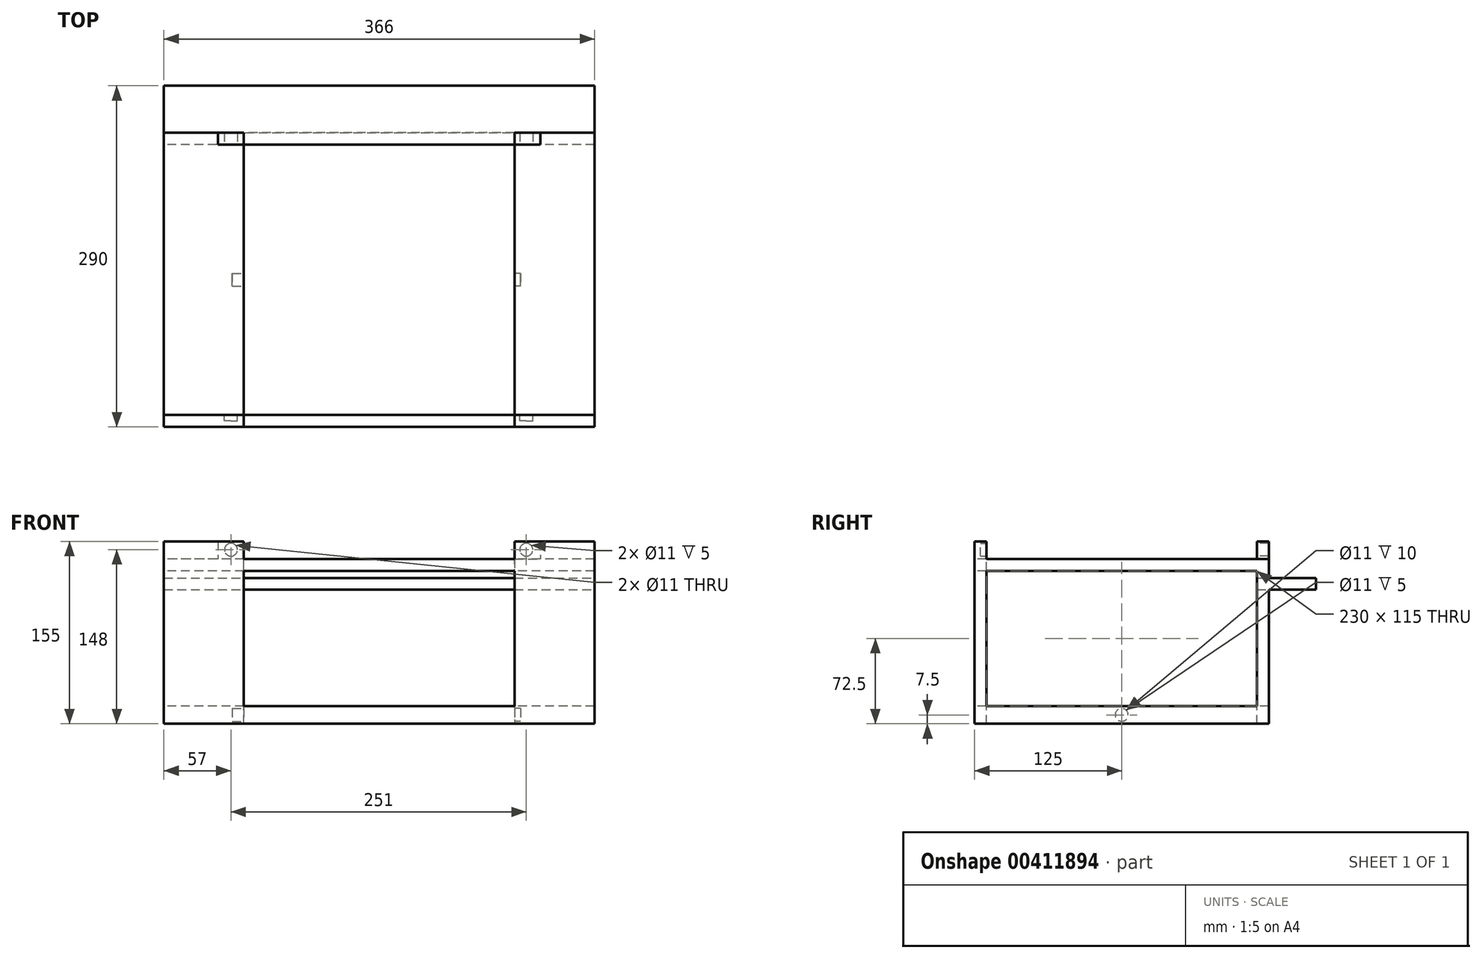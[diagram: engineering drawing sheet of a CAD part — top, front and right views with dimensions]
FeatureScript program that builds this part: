
annotation { "Feature Type Name" : "Feature", "Feature Type Description" : "" }
export const myFeature = defineFeature(function(context is Context, id is Id, definition is map)
    precondition{}
    {
        {
            var Q0;
            Q0=qCreatedBy(makeId("Top.planeOp"),FACE);
            var sketch = newSketch(context, id + "F0", { "sketchPlane" : qUnion([Q0])});
            skLineSegment(sketch, "E0.bottom", {"start": v(-183, 125) * mm, "end": v(183, 125) * mm});
            skLineSegment(sketch, "E0.top", {"start": v(-183, -125) * mm, "end": v(183, -125) * mm});
            skLineSegment(sketch, "E0.left", {"start": v(-183, 125) * mm, "end": v(-183, -125) * mm});
            skLineSegment(sketch, "E0.right", {"start": v(183, 125) * mm, "end": v(183, -125) * mm});
            skSolve(sketch);
        }
        {
            var Q0;
            Q0 = qSketchRegion(id + "F0", true);
            extrude(context, id + "F1", {"entities" : qUnion([Q0]), "depth" : 155 * mm});
        }
        {
            var Q0;
            Q0=makeQuery(id+"F1.opExtrude","CAP_FACE",FACE,{"disambiguationData":[OSD([sQuery(id+"F0.wireOp",EDGE,"E0.bottom"),sQuery(id+"F0.wireOp",EDGE,"E0.top"),sQuery(id+"F0.wireOp",EDGE,"E0.left"),sQuery(id+"F0.wireOp",EDGE,"E0.right")])],"isStart":false});
            shell(context, id + "F2", {"entities" : qUnion([Q0]), "thickness" : 10 * mm});
        }
        {
            var Q0;
            Q0=makeQuery(id+"F2.opShell","OFFSET_FACE",FACE,{"disambiguationData":[OSD([sQuery(id+"F0.wireOp",EDGE,"E0.bottom"),sQuery(id+"F0.wireOp",EDGE,"E0.top"),sQuery(id+"F0.wireOp",EDGE,"E0.left"),sQuery(id+"F0.wireOp",EDGE,"E0.right")])]});
            var sketch = newSketch(context, id + "F3", { "sketchPlane" : qUnion([Q0])});
            skSolve(sketch);
        }
        {
            var Q0;
            Q0 = qSketchRegion(id + "F3", true);
            var Q1;
            {var subQ0=sQuery(id+"F0.wireOp",EDGE,"E0.bottom");Q1=makeQuery(id+"F3.imprint","IMPRINT",FACE,{"disambiguationData":[TD([[makeQuery(id+"F3.imprint","IMPRINT",EDGE,{"derivedFrom":makeQuery(id+"F2.opShell","OFFSET_EDGE",EDGE,{"disambiguationData":[OSD([subQ0]),TDD([makeQuery(id+"F1.opExtrude","CAP_EDGE",EDGE,{"disambiguationData":[OSD([subQ0])],"isStart":true})])]})}),-1.0]])]});}
            extrude(context, id + "F4", {"entities" : qUnion([Q0, Q1]), "operationType" : NewBodyOperationType.REMOVE, "oppositeDirection" : true, "depth" : 25 * mm});
        }
        {
            var Q0;
            Q0=makeQuery(id+"F1.opExtrude","SWEPT_FACE",FACE,{"disambiguationData":[OSD([sQuery(id+"F0.wireOp",EDGE,"E0.top")])]});
            var sketch = newSketch(context, id + "F5", { "sketchPlane" : qUnion([Q0])});
            skLineSegment(sketch, "E1", {"start": v(0, 0) * mm, "end": v(0, 92.09) * mm});
            skLineSegment(sketch, "E2.bottom", {"start": v(-115, 130) * mm, "end": v(115, 130) * mm});
            skLineSegment(sketch, "E2.top", {"start": v(-115, 15) * mm, "end": v(115, 15) * mm});
            skLineSegment(sketch, "E2.left", {"start": v(-115, 130) * mm, "end": v(-115, 15) * mm});
            skLineSegment(sketch, "E2.right", {"start": v(115, 130) * mm, "end": v(115, 15) * mm});
            skLineSegment(sketch, "E3.bottom", {"start": v(-115, 155) * mm, "end": v(115, 155) * mm});
            skLineSegment(sketch, "E3.top", {"start": v(-115, 140) * mm, "end": v(115, 140) * mm});
            skLineSegment(sketch, "E3.left", {"start": v(-115, 155) * mm, "end": v(-115, 140) * mm});
            skLineSegment(sketch, "E3.right", {"start": v(115, 155) * mm, "end": v(115, 140) * mm});
            skSolve(sketch);
        }
        {
            var Q0;
            Q0 = qSketchRegion(id + "F5", true);
            extrude(context, id + "F6", {"entities" : qUnion([Q0]), "operationType" : NewBodyOperationType.REMOVE, "oppositeDirection" : true, "depth" : 500 * mm});
        }
        {
            var Q0;
            Q0=makeQuery(id+"F1.opExtrude","SWEPT_FACE",FACE,{"disambiguationData":[OSD([sQuery(id+"F0.wireOp",EDGE,"E0.left")])]});
            var sketch = newSketch(context, id + "F7", { "sketchPlane" : qUnion([Q0])});
            skLineSegment(sketch, "E4", {"start": v(0, 0) * mm, "end": v(0, 112.83) * mm});
            skLineSegment(sketch, "E5.bottom", {"start": v(-115, 130) * mm, "end": v(115, 130) * mm});
            skLineSegment(sketch, "E5.top", {"start": v(-115, 15) * mm, "end": v(115, 15) * mm});
            skLineSegment(sketch, "E5.left", {"start": v(-115, 130) * mm, "end": v(-115, 15) * mm});
            skLineSegment(sketch, "E5.right", {"start": v(115, 130) * mm, "end": v(115, 15) * mm});
            skLineSegment(sketch, "E6.bottom", {"start": v(-125, 114) * mm, "end": v(-125, 114) * mm});
            skLineSegment(sketch, "E6.top", {"start": v(-125, 0) * mm, "end": v(-125, 0) * mm});
            skLineSegment(sketch, "E7.bottom", {"start": v(-125, 155) * mm, "end": v(115, 155) * mm});
            skLineSegment(sketch, "E7.top", {"start": v(-125, 140) * mm, "end": v(115, 140) * mm});
            skLineSegment(sketch, "E7.left", {"start": v(-125, 155) * mm, "end": v(-125, 140) * mm});
            skLineSegment(sketch, "E7.right", {"start": v(115, 155) * mm, "end": v(115, 140) * mm});
            skSolve(sketch);
        }
        {
            var Q0;
            Q0=makeQuery(id+"F7.imprint","IMPRINT",FACE,{"disambiguationData":[TD([[makeQuery(id+"F7.imprint","IMPRINT",EDGE,{"derivedFrom":sQuery(id+"F7.wireOp",EDGE,"E7.bottom")}),-1.0]])]});
            var Q1;
            Q1=makeQuery(id+"F7.imprint","IMPRINT",FACE,{"disambiguationData":[TD([[makeQuery(id+"F7.imprint","IMPRINT",EDGE,{"derivedFrom":sQuery(id+"F7.wireOp",EDGE,"E5.bottom")}),-1.0]])]});
            extrude(context, id + "F8", {"entities" : qUnion([Q0, Q1]), "operationType" : NewBodyOperationType.REMOVE, "oppositeDirection" : true, "depth" : 500 * mm});
        }
        {
            var Q0;
            Q0=makeQuery(id+"F1.opExtrude","SWEPT_FACE",FACE,{"disambiguationData":[OSD([sQuery(id+"F0.wireOp",EDGE,"E0.left")])]});
            var sketch = newSketch(context, id + "F9", { "sketchPlane" : qUnion([Q0])});
            skLineSegment(sketch, "E8.bottom", {"start": v(-115, 124) * mm, "end": v(-165, 124) * mm});
            skLineSegment(sketch, "E8.top", {"start": v(-115, 114) * mm, "end": v(-165, 114) * mm});
            skLineSegment(sketch, "E8.left", {"start": v(-115, 124) * mm, "end": v(-115, 114) * mm});
            skLineSegment(sketch, "E8.right", {"start": v(-165, 124) * mm, "end": v(-165, 114) * mm});
            skLineSegment(sketch, "E9.0", {"start": v(115, 155) * mm, "end": v(125, 155) * mm});
            skLineSegment(sketch, "E10.0", {"start": v(125, 155) * mm, "end": v(125, 0) * mm});
            skSolve(sketch);
        }
        {
            var Q0;
            Q0 = qSketchRegion(id + "F9", true);
            var Q1;
            Q1=makeQuery(id+"F1.opExtrude","SWEPT_FACE",FACE,{"disambiguationData":[OSD([sQuery(id+"F0.wireOp",EDGE,"E0.right")])]});
            extrude(context, id + "F10", {"entities" : qUnion([Q0]), "operationType" : NewBodyOperationType.ADD, "endBound" : BoundingType.UP_TO_SURFACE, "oppositeDirection" : true, "endBoundEntityFace" : qUnion([Q1]), "depth" : 25 * mm});
        }
        {
            var Q0;
            {var subQ0=sQuery(id+"F0.wireOp",EDGE,"E0.bottom");var subQ1=makeQuery(id+"F1.opExtrude","SWEPT_FACE",FACE,{"disambiguationData":[OSD([subQ0])]});var subQ9=sQuery(id+"F9.wireOp",EDGE,"E8.bottom");Q0=makeQuery(id+"F10.boolean.opBoolean","SPLIT",FACE,{"disambiguationData":[TD([makeQuery(id+"F10.opExtrude","SWEPT_FACE",FACE,{"disambiguationData":[OSD([subQ9])]})])],"derivedFrom":subQ1});}
            var sketch = newSketch(context, id + "F11", { "sketchPlane" : qUnion([Q0])});
            skLineSegment(sketch, "E11.bottom", {"start": v(-115, 124) * mm, "end": v(115, 124) * mm});
            skLineSegment(sketch, "E11.top", {"start": v(-115, 150.02) * mm, "end": v(115, 150.02) * mm});
            skLineSegment(sketch, "E11.left", {"start": v(-115, 124) * mm, "end": v(-115, 150.02) * mm});
            skLineSegment(sketch, "E11.right", {"start": v(115, 124) * mm, "end": v(115, 150.02) * mm});
            skSolve(sketch);
        }
        {
            var Q0;
            {var subQ0=sQuery(id+"F11.wireOp",EDGE,"E11.bottom");Q0=makeQuery(id+"F11.imprint","IMPRINT",FACE,{"disambiguationData":[TD([[makeQuery(id+"F11.imprint","IMPRINT",EDGE,{"derivedFrom":subQ0}),1.0]])]});}
            var Q1;
            {var subQ1=sQuery(id+"F0.wireOp",EDGE,"E0.bottom");var subQ2=makeQuery(id+"F1.opExtrude","SWEPT_FACE",FACE,{"disambiguationData":[OSD([subQ1])]});var subQ3=makeQuery(id+"F6.boolean.opBoolean","INTERSECT",EDGE,{"derivedFrom":[subQ2,makeQuery(id+"F6.opExtrude","SWEPT_FACE",FACE,{"disambiguationData":[OSD([sQuery(id+"F5.wireOp",EDGE,"E2.bottom")])]})]});Q1=makeQuery(id+"F11.imprint","IMPRINT",FACE,{"disambiguationData":[TD([[makeQuery(id+"F11.imprint","IMPRINT",EDGE,{"derivedFrom":subQ3}),1.0]])]});}
            extrude(context, id + "F12", {"entities" : qUnion([Q0, Q1]), "operationType" : NewBodyOperationType.REMOVE, "oppositeDirection" : true, "depth" : 200 * mm});
        }
        {
            var Q0;
            {var subQ0=sQuery(id+"F0.wireOp",EDGE,"E0.right");var subQ2=sQuery(id+"F0.wireOp",EDGE,"E0.bottom");var subQ4=makeQuery(id+"F1.opExtrude","SWEPT_FACE",FACE,{"disambiguationData":[OSD([subQ2])]});Q0=makeQuery(id+"F12.boolean.opBoolean","SPLIT",FACE,{"disambiguationData":[TD([makeQuery(id+"F1.opExtrude","SWEPT_FACE",FACE,{"disambiguationData":[OSD([subQ0])]})])],"derivedFrom":makeQuery(id+"F8.boolean.opBoolean","MERGE",FACE,{"derivedFrom":[makeQuery(id+"F6.boolean.opBoolean","COPY",FACE,{"disambiguationData":[TD([subQ4])],"derivedFrom":makeQuery(id+"F6.opExtrude","SWEPT_FACE",FACE,{"disambiguationData":[OSD([sQuery(id+"F5.wireOp",EDGE,"E3.top")])]})}),makeQuery(id+"F8.opExtrude","SWEPT_FACE",FACE,{"disambiguationData":[OSD([sQuery(id+"F7.wireOp",EDGE,"E7.top")])]})]})});}
            var sketch = newSketch(context, id + "F13", { "sketchPlane" : qUnion([Q0])});
            skLineSegment(sketch, "E12.bottom", {"start": v(115, 115) * mm, "end": v(137, 115) * mm});
            skLineSegment(sketch, "E12.top", {"start": v(115, 125) * mm, "end": v(137, 125) * mm});
            skLineSegment(sketch, "E12.left", {"start": v(115, 115) * mm, "end": v(115, 125) * mm});
            skLineSegment(sketch, "E12.right", {"start": v(137, 115) * mm, "end": v(137, 125) * mm});
            skSolve(sketch);
        }
        {
            var Q0;
            Q0=makeQuery(id+"F13.imprint","IMPRINT",FACE,{"disambiguationData":[TD([[makeQuery(id+"F13.imprint","IMPRINT",EDGE,{"derivedFrom":sQuery(id+"F13.wireOp",EDGE,"E12.bottom")}),-1.0]])]});
            extrude(context, id + "F14", {"entities" : qUnion([Q0]), "operationType" : NewBodyOperationType.ADD, "depth" : 15 * mm});
        }
        {
            var Q0;
            {var subQ0=sQuery(id+"F0.wireOp",EDGE,"E0.bottom");var subQ3=makeQuery(id+"F1.opExtrude","SWEPT_FACE",FACE,{"disambiguationData":[OSD([subQ0])]});var subQ4=sQuery(id+"F0.wireOp",EDGE,"E0.left");Q0=makeQuery(id+"F12.boolean.opBoolean","SPLIT",FACE,{"disambiguationData":[TD([makeQuery(id+"F1.opExtrude","SWEPT_FACE",FACE,{"disambiguationData":[OSD([subQ4])]})])],"derivedFrom":makeQuery(id+"F8.boolean.opBoolean","MERGE",FACE,{"derivedFrom":[makeQuery(id+"F6.boolean.opBoolean","COPY",FACE,{"disambiguationData":[TD([subQ3])],"derivedFrom":makeQuery(id+"F6.opExtrude","SWEPT_FACE",FACE,{"disambiguationData":[OSD([sQuery(id+"F5.wireOp",EDGE,"E3.top")])]})}),makeQuery(id+"F8.opExtrude","SWEPT_FACE",FACE,{"disambiguationData":[OSD([sQuery(id+"F7.wireOp",EDGE,"E7.top")])]})]})});}
            var sketch = newSketch(context, id + "F15", { "sketchPlane" : qUnion([Q0])});
            skLineSegment(sketch, "E13.bottom", {"start": v(-115, 115) * mm, "end": v(-137, 115) * mm});
            skLineSegment(sketch, "E13.top", {"start": v(-115, 125) * mm, "end": v(-137, 125) * mm});
            skLineSegment(sketch, "E13.left", {"start": v(-115, 115) * mm, "end": v(-115, 125) * mm});
            skLineSegment(sketch, "E13.right", {"start": v(-137, 115) * mm, "end": v(-137, 125) * mm});
            skSolve(sketch);
        }
        {
            var Q0;
            Q0=makeQuery(id+"F15.imprint","IMPRINT",FACE,{"disambiguationData":[TD([[makeQuery(id+"F15.imprint","IMPRINT",EDGE,{"derivedFrom":sQuery(id+"F15.wireOp",EDGE,"E13.bottom")}),-1.0]])]});
            extrude(context, id + "F16", {"entities" : qUnion([Q0]), "operationType" : NewBodyOperationType.ADD, "depth" : 15 * mm});
        }
        {
            var Q0;
            {var subQ4=sQuery(id+"F0.wireOp",EDGE,"E0.right");Q0=makeQuery(id+"F8.boolean.opBoolean","SPLIT",FACE,{"disambiguationData":[TD([makeQuery(id+"F8.opExtrude","SWEPT_FACE",FACE,{"disambiguationData":[OSD([sQuery(id+"F7.wireOp",EDGE,"E5.bottom")])]})])],"derivedFrom":makeQuery(id+"F4.boolean.opBoolean","MERGE",FACE,{"derivedFrom":[makeQuery(id+"F2.opShell","OFFSET_FACE",FACE,{"disambiguationData":[OSD([subQ4])]}),makeQuery(id+"F4.opExtrude","SWEPT_FACE",FACE,{"disambiguationData":[OSD([subQ4])]})]})});}
            var Q1;
            {var subQ0=sQuery(id+"F0.wireOp",EDGE,"E0.top");Q1=makeQuery(id+"F6.boolean.opBoolean","COPY",FACE,{"disambiguationData":[TD([makeQuery(id+"F1.opExtrude","SWEPT_FACE",FACE,{"disambiguationData":[OSD([subQ0])]})])],"derivedFrom":makeQuery(id+"F6.opExtrude","SWEPT_FACE",FACE,{"disambiguationData":[OSD([sQuery(id+"F5.wireOp",EDGE,"E2.right")])]})});}
            extrude(context, id + "F17", {"entities" : qUnion([Q0]), "operationType" : NewBodyOperationType.ADD, "endBound" : BoundingType.UP_TO_SURFACE, "endBoundEntityFace" : qUnion([Q1]), "depth" : 25 * mm});
        }
        {
            var Q0;
            {var subQ4=sQuery(id+"F0.wireOp",EDGE,"E0.left");Q0=makeQuery(id+"F8.boolean.opBoolean","SPLIT",FACE,{"disambiguationData":[TD([makeQuery(id+"F8.opExtrude","SWEPT_FACE",FACE,{"disambiguationData":[OSD([sQuery(id+"F7.wireOp",EDGE,"E5.bottom")])]})])],"derivedFrom":makeQuery(id+"F4.boolean.opBoolean","MERGE",FACE,{"derivedFrom":[makeQuery(id+"F2.opShell","OFFSET_FACE",FACE,{"disambiguationData":[OSD([subQ4])]}),makeQuery(id+"F4.opExtrude","SWEPT_FACE",FACE,{"disambiguationData":[OSD([subQ4])]})]})});}
            var Q1;
            {var subQ0=sQuery(id+"F0.wireOp",EDGE,"E0.top");Q1=makeQuery(id+"F6.boolean.opBoolean","COPY",FACE,{"disambiguationData":[TD([makeQuery(id+"F1.opExtrude","SWEPT_FACE",FACE,{"disambiguationData":[OSD([subQ0])]})])],"derivedFrom":makeQuery(id+"F6.opExtrude","SWEPT_FACE",FACE,{"disambiguationData":[OSD([sQuery(id+"F5.wireOp",EDGE,"E2.left")])]})});}
            extrude(context, id + "F18", {"entities" : qUnion([Q0]), "operationType" : NewBodyOperationType.ADD, "endBound" : BoundingType.UP_TO_SURFACE, "endBoundEntityFace" : qUnion([Q1]), "depth" : 25 * mm});
        }
        {
            var Q0;
            {var subQ2=sQuery(id+"F0.wireOp",EDGE,"E0.right");Q0=makeQuery(id+"F8.boolean.opBoolean","SPLIT",FACE,{"disambiguationData":[TD([makeQuery(id+"F8.opExtrude","SWEPT_FACE",FACE,{"disambiguationData":[OSD([sQuery(id+"F7.wireOp",EDGE,"E5.top")])]})])],"derivedFrom":makeQuery(id+"F4.boolean.opBoolean","MERGE",FACE,{"derivedFrom":[makeQuery(id+"F2.opShell","OFFSET_FACE",FACE,{"disambiguationData":[OSD([subQ2])]}),makeQuery(id+"F4.opExtrude","SWEPT_FACE",FACE,{"disambiguationData":[OSD([subQ2])]})]})});}
            var Q1;
            {var subQ0=sQuery(id+"F0.wireOp",EDGE,"E0.top");Q1=makeQuery(id+"F6.boolean.opBoolean","COPY",FACE,{"disambiguationData":[TD([makeQuery(id+"F1.opExtrude","SWEPT_FACE",FACE,{"disambiguationData":[OSD([subQ0])]})])],"derivedFrom":makeQuery(id+"F6.opExtrude","SWEPT_FACE",FACE,{"disambiguationData":[OSD([sQuery(id+"F5.wireOp",EDGE,"E2.right")])]})});}
            extrude(context, id + "F19", {"entities" : qUnion([Q0]), "operationType" : NewBodyOperationType.ADD, "endBound" : BoundingType.UP_TO_SURFACE, "endBoundEntityFace" : qUnion([Q1]), "depth" : 25 * mm});
        }
        {
            var Q0;
            {var subQ2=sQuery(id+"F0.wireOp",EDGE,"E0.left");Q0=makeQuery(id+"F8.boolean.opBoolean","SPLIT",FACE,{"disambiguationData":[TD([makeQuery(id+"F8.opExtrude","SWEPT_FACE",FACE,{"disambiguationData":[OSD([sQuery(id+"F7.wireOp",EDGE,"E5.top")])]})])],"derivedFrom":makeQuery(id+"F4.boolean.opBoolean","MERGE",FACE,{"derivedFrom":[makeQuery(id+"F2.opShell","OFFSET_FACE",FACE,{"disambiguationData":[OSD([subQ2])]}),makeQuery(id+"F4.opExtrude","SWEPT_FACE",FACE,{"disambiguationData":[OSD([subQ2])]})]})});}
            var Q1;
            {var subQ0=sQuery(id+"F0.wireOp",EDGE,"E0.top");Q1=makeQuery(id+"F6.boolean.opBoolean","COPY",FACE,{"disambiguationData":[TD([makeQuery(id+"F1.opExtrude","SWEPT_FACE",FACE,{"disambiguationData":[OSD([subQ0])]})])],"derivedFrom":makeQuery(id+"F6.opExtrude","SWEPT_FACE",FACE,{"disambiguationData":[OSD([sQuery(id+"F5.wireOp",EDGE,"E2.left")])]})});}
            extrude(context, id + "F20", {"entities" : qUnion([Q0]), "operationType" : NewBodyOperationType.ADD, "endBound" : BoundingType.UP_TO_SURFACE, "endBoundEntityFace" : qUnion([Q1]), "depth" : 25 * mm});
        }
        {
            var Q0;
            {var subQ2=sQuery(id+"F13.wireOp",EDGE,"E12.right");var subQ3=sQuery(id+"F13.wireOp",EDGE,"E12.bottom");var subQ4=sQuery(id+"F0.wireOp",EDGE,"E0.bottom");var subQ6=makeQuery(id+"F2.opShell","OFFSET_FACE",FACE,{"disambiguationData":[OSD([subQ4])]});Q0=makeQuery(id+"F17.boolean.opBoolean","SPLIT",FACE,{"disambiguationData":[TD([makeQuery(id+"F14.opExtrude","SWEPT_FACE",FACE,{"disambiguationData":[OSD([subQ2])]})])],"derivedFrom":makeQuery(id+"F16.boolean.opBoolean","MERGE",FACE,{"derivedFrom":[makeQuery(id+"F14.boolean.opBoolean","MERGE",FACE,{"derivedFrom":[makeQuery(id+"F10.boolean.opBoolean","MERGE",FACE,{"derivedFrom":[makeQuery(id+"F8.boolean.opBoolean","MERGE",FACE,{"derivedFrom":[makeQuery(id+"F4.boolean.opBoolean","MERGE",FACE,{"derivedFrom":[subQ6],"fromTools":[makeQuery(id+"F4.opExtrude","SWEPT_FACE",FACE,{"disambiguationData":[OSD([subQ4])]})]})],"fromTools":[makeQuery(id+"F8.opExtrude","SWEPT_FACE",FACE,{"disambiguationData":[OSD([sQuery(id+"F7.wireOp",EDGE,"E5.left")])]})]}),makeQuery(id+"F10.opExtrude","SWEPT_FACE",FACE,{"disambiguationData":[OSD([sQuery(id+"F9.wireOp",EDGE,"E8.left")])]})]}),makeQuery(id+"F14.opExtrude","SWEPT_FACE",FACE,{"disambiguationData":[OSD([subQ3])]})]}),makeQuery(id+"F16.opExtrude","SWEPT_FACE",FACE,{"disambiguationData":[OSD([sQuery(id+"F15.wireOp",EDGE,"E13.bottom")])]})]})});}
            var sketch = newSketch(context, id + "F21", { "sketchPlane" : qUnion([Q0])});
            skCircle(sketch, "E14", {"center": v(125, 148) * mm, "radius": 5.5 * mm});
            skLineSegment(sketch, "E15.0.0", {"start": v(115, 155) * mm, "end": v(115, 140) * mm});
            skLineSegment(sketch, "E15.0.1", {"start": v(115, 140) * mm, "end": v(137, 140) * mm});
            skLineSegment(sketch, "E15.0.2", {"start": v(137, 140) * mm, "end": v(137, 155) * mm});
            skLineSegment(sketch, "E15.0.3", {"start": v(137, 155) * mm, "end": v(115, 155) * mm});
            skSolve(sketch);
        }
        {
            var Q0;
            Q0=makeQuery(id+"F21.imprint","IMPRINT",FACE,{"disambiguationData":[TD([[makeQuery(id+"F21.imprint","IMPRINT",EDGE,{"derivedFrom":sQuery(id+"F21.wireOp",EDGE,"E14")}),1.0]])]});
            extrude(context, id + "F22", {"entities" : qUnion([Q0]), "operationType" : NewBodyOperationType.REMOVE, "depth" : 235 * mm});
        }
        {
            var Q0;
            {var subQ2=sQuery(id+"F0.wireOp",EDGE,"E0.bottom");var subQ4=makeQuery(id+"F2.opShell","OFFSET_FACE",FACE,{"disambiguationData":[OSD([subQ2])]});var subQ6=sQuery(id+"F15.wireOp",EDGE,"E13.right");var subQ7=makeQuery(id+"F16.opExtrude","SWEPT_FACE",FACE,{"disambiguationData":[OSD([subQ6])]});var subQ8=sQuery(id+"F15.wireOp",EDGE,"E13.bottom");var subQ14=sQuery(id+"F0.wireOp",EDGE,"E0.left");var subQ21=sQuery(id+"F9.wireOp",EDGE,"E8.left");var subQ26=makeQuery(id+"F8.opExtrude","SWEPT_FACE",FACE,{"disambiguationData":[OSD([sQuery(id+"F7.wireOp",EDGE,"E5.left")])]});var subQ30=makeQuery(id+"F1.opExtrude","SWEPT_FACE",FACE,{"disambiguationData":[OSD([subQ14])]});Q0=makeQuery(id+"F18.boolean.opBoolean","SPLIT",FACE,{"disambiguationData":[TD([subQ7])],"derivedFrom":makeQuery(id+"F17.boolean.opBoolean","SPLIT",FACE,{"disambiguationData":[TD([subQ30])],"derivedFrom":makeQuery(id+"F16.boolean.opBoolean","MERGE",FACE,{"derivedFrom":[makeQuery(id+"F14.boolean.opBoolean","MERGE",FACE,{"derivedFrom":[makeQuery(id+"F10.boolean.opBoolean","MERGE",FACE,{"derivedFrom":[makeQuery(id+"F8.boolean.opBoolean","MERGE",FACE,{"derivedFrom":[makeQuery(id+"F4.boolean.opBoolean","MERGE",FACE,{"derivedFrom":[subQ4],"fromTools":[makeQuery(id+"F4.opExtrude","SWEPT_FACE",FACE,{"disambiguationData":[OSD([subQ2])]})]})],"fromTools":[subQ26]}),makeQuery(id+"F10.opExtrude","SWEPT_FACE",FACE,{"disambiguationData":[OSD([subQ21])]})]}),makeQuery(id+"F14.opExtrude","SWEPT_FACE",FACE,{"disambiguationData":[OSD([sQuery(id+"F13.wireOp",EDGE,"E12.bottom")])]})]}),makeQuery(id+"F16.opExtrude","SWEPT_FACE",FACE,{"disambiguationData":[OSD([subQ8])]})]})})});}
            var sketch = newSketch(context, id + "F23", { "sketchPlane" : qUnion([Q0])});
            skCircle(sketch, "E16", {"center": v(-126, 148) * mm, "radius": 5.5 * mm});
            skPoint(sketch, "E16.centerSnap0", {"position": v(-126, 155) * mm});
            skLineSegment(sketch, "E17.0.0", {"start": v(-137, 140) * mm, "end": v(-115, 140) * mm});
            skLineSegment(sketch, "E17.0.1", {"start": v(-115, 140) * mm, "end": v(-115, 155) * mm});
            skLineSegment(sketch, "E17.0.2", {"start": v(-115, 155) * mm, "end": v(-137, 155) * mm});
            skLineSegment(sketch, "E17.0.3", {"start": v(-137, 155) * mm, "end": v(-137, 140) * mm});
            skSolve(sketch);
        }
        {
            var Q0;
            Q0=makeQuery(id+"F23.imprint","IMPRINT",FACE,{"disambiguationData":[TD([[makeQuery(id+"F23.imprint","IMPRINT",EDGE,{"derivedFrom":sQuery(id+"F23.wireOp",EDGE,"E16")}),1.0]])]});
            extrude(context, id + "F24", {"entities" : qUnion([Q0]), "operationType" : NewBodyOperationType.REMOVE, "oppositeDirection" : true, "depth" : 25 * mm});
        }
        {
            var Q0;
            Q0=makeQuery(id+"F19.opExtrude","CAP_FACE",FACE,{"disambiguationData":[OSD([sQuery(id+"F0.wireOp",EDGE,"E0.right")])],"isStart":false});
            var sketch = newSketch(context, id + "F25", { "sketchPlane" : qUnion([Q0])});
            skCircle(sketch, "E18", {"center": v(0, 7.5) * mm, "radius": 5.5 * mm});
            skLineSegment(sketch, "E19.0.0", {"start": v(-125, 140) * mm, "end": v(-125, 124) * mm});
            skLineSegment(sketch, "E19.0.1", {"start": v(-125, 124) * mm, "end": v(-165, 124) * mm});
            skLineSegment(sketch, "E19.0.2", {"start": v(-165, 124) * mm, "end": v(-165, 114) * mm});
            skLineSegment(sketch, "E19.0.3", {"start": v(-165, 114) * mm, "end": v(-125, 114) * mm});
            skLineSegment(sketch, "E19.0.4", {"start": v(-125, 114) * mm, "end": v(-125, 0) * mm});
            skLineSegment(sketch, "E19.0.5", {"start": v(-125, 0) * mm, "end": v(125, 0) * mm});
            skLineSegment(sketch, "E19.0.6", {"start": v(125, 0) * mm, "end": v(125, 155) * mm});
            skLineSegment(sketch, "E19.0.7", {"start": v(125, 155) * mm, "end": v(115, 155) * mm});
            skLineSegment(sketch, "E19.0.8", {"start": v(115, 155) * mm, "end": v(115, 140) * mm});
            skLineSegment(sketch, "E19.0.9", {"start": v(115, 140) * mm, "end": v(-125, 140) * mm});
            skSolve(sketch);
        }
        {
            var Q0;
            Q0=makeQuery(id+"F25.imprint","IMPRINT",FACE,{"disambiguationData":[TD([[makeQuery(id+"F25.imprint","IMPRINT",EDGE,{"derivedFrom":sQuery(id+"F25.wireOp",EDGE,"E18")}),1.0]])]});
            extrude(context, id + "F26", {"entities" : qUnion([Q0]), "operationType" : NewBodyOperationType.REMOVE, "depth" : 240 * mm});
        }
        {
            var Q0;
            Q0=makeQuery(id+"F22.boolean.opBoolean","COPY",FACE,{"derivedFrom":makeQuery(id+"F22.opExtrude","CAP_FACE",FACE,{"disambiguationData":[OSD([sQuery(id+"F21.wireOp",EDGE,"E14")])],"isStart":false})});
            extrude(context, id + "F27", {"entities" : qUnion([Q0]), "operationType" : NewBodyOperationType.REMOVE, "depth" : 260 * mm});
        }
        {
            var Q0;
            {var subQ2=sQuery(id+"F0.wireOp",EDGE,"E0.bottom");var subQ4=makeQuery(id+"F2.opShell","OFFSET_FACE",FACE,{"disambiguationData":[OSD([subQ2])]});var subQ6=sQuery(id+"F15.wireOp",EDGE,"E13.right");var subQ7=makeQuery(id+"F16.opExtrude","SWEPT_FACE",FACE,{"disambiguationData":[OSD([subQ6])]});var subQ8=sQuery(id+"F15.wireOp",EDGE,"E13.bottom");var subQ14=sQuery(id+"F0.wireOp",EDGE,"E0.left");var subQ21=sQuery(id+"F9.wireOp",EDGE,"E8.left");var subQ26=makeQuery(id+"F8.opExtrude","SWEPT_FACE",FACE,{"disambiguationData":[OSD([sQuery(id+"F7.wireOp",EDGE,"E5.left")])]});var subQ30=makeQuery(id+"F1.opExtrude","SWEPT_FACE",FACE,{"disambiguationData":[OSD([subQ14])]});Q0=makeQuery(id+"F18.boolean.opBoolean","SPLIT",FACE,{"disambiguationData":[TD([subQ7])],"derivedFrom":makeQuery(id+"F17.boolean.opBoolean","SPLIT",FACE,{"disambiguationData":[TD([subQ30])],"derivedFrom":makeQuery(id+"F16.boolean.opBoolean","MERGE",FACE,{"derivedFrom":[makeQuery(id+"F14.boolean.opBoolean","MERGE",FACE,{"derivedFrom":[makeQuery(id+"F10.boolean.opBoolean","MERGE",FACE,{"derivedFrom":[makeQuery(id+"F8.boolean.opBoolean","MERGE",FACE,{"derivedFrom":[makeQuery(id+"F4.boolean.opBoolean","MERGE",FACE,{"derivedFrom":[subQ4],"fromTools":[makeQuery(id+"F4.opExtrude","SWEPT_FACE",FACE,{"disambiguationData":[OSD([subQ2])]})]})],"fromTools":[subQ26]}),makeQuery(id+"F10.opExtrude","SWEPT_FACE",FACE,{"disambiguationData":[OSD([subQ21])]})]}),makeQuery(id+"F14.opExtrude","SWEPT_FACE",FACE,{"disambiguationData":[OSD([sQuery(id+"F13.wireOp",EDGE,"E12.bottom")])]})]}),makeQuery(id+"F16.opExtrude","SWEPT_FACE",FACE,{"disambiguationData":[OSD([subQ8])]})]})})});}
            var sketch = newSketch(context, id + "F28", { "sketchPlane" : qUnion([Q0])});
            skCircle(sketch, "E20.0", {"center": v(-126, 148) * mm, "radius": 5.5 * mm});
            skSolve(sketch);
        }
        {
            var Q0;
            Q0=makeQuery(id+"F28.imprint","IMPRINT",FACE,{"disambiguationData":[TD([[makeQuery(id+"F28.imprint","IMPRINT",EDGE,{"derivedFrom":sQuery(id+"F28.wireOp",EDGE,"E20.0")}),1.0]])]});
            extrude(context, id + "F29", {"entities" : qUnion([Q0]), "operationType" : NewBodyOperationType.REMOVE, "depth" : 235 * mm});
        }
        {
            var Q0;
            Q0=makeQuery(id+"F19.opExtrude","CAP_FACE",FACE,{"disambiguationData":[OSD([sQuery(id+"F0.wireOp",EDGE,"E0.right")])],"isStart":false});
            var sketch = newSketch(context, id + "F30", { "sketchPlane" : qUnion([Q0])});
            skCircle(sketch, "E21", {"center": v(0, 7.5) * mm, "radius": 5.5 * mm});
            skSolve(sketch);
        }
        {
            var Q0;
            Q0 = qSketchRegion(id + "F30", true);
            extrude(context, id + "F31", {"entities" : qUnion([Q0]), "operationType" : NewBodyOperationType.REMOVE, "oppositeDirection" : true, "depth" : 5 * mm});
        }
    });
